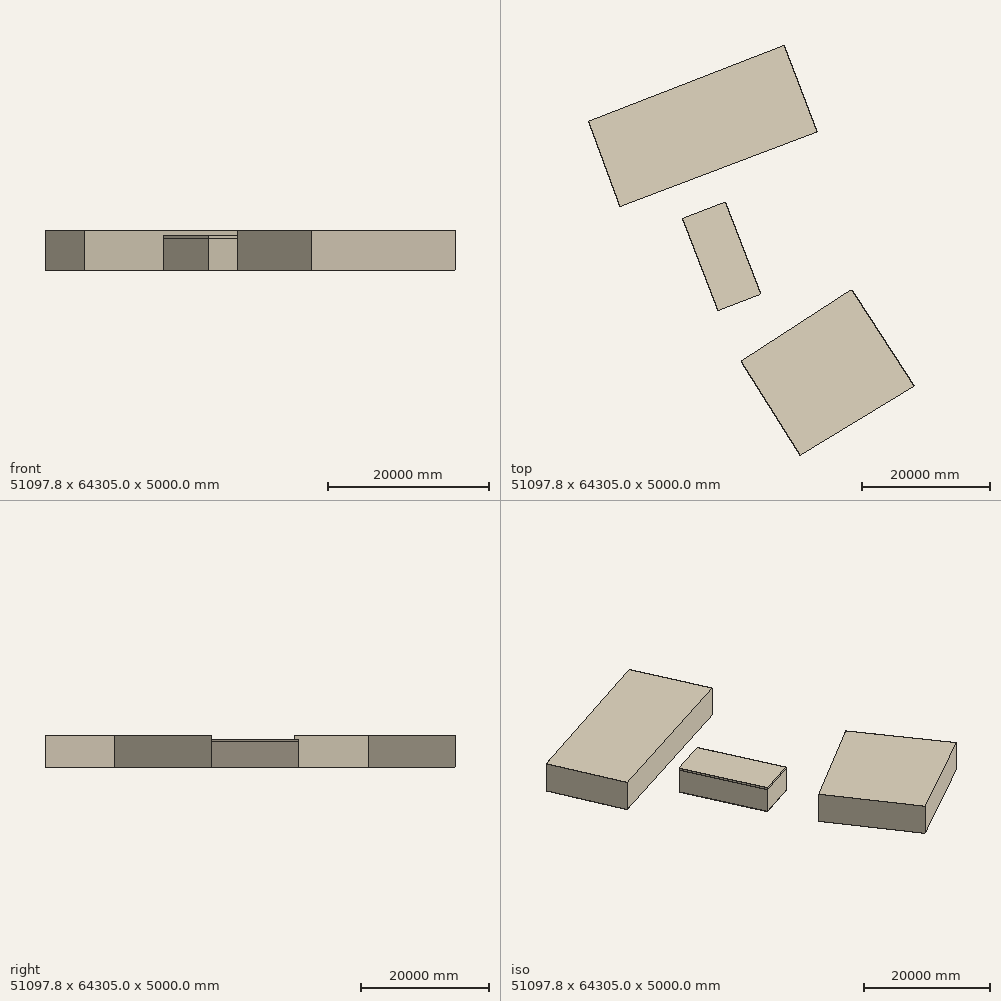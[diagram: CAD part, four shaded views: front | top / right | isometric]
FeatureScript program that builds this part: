
annotation { "Feature Type Name" : "Feature", "Feature Type Description" : "" }
export const myFeature = defineFeature(function(context is Context, id is Id, definition is map)
    precondition{}
    {
        {
            var Q0;
            Q0=qCreatedBy(makeId("Top.planeOp"),FACE);
            var sketch = newSketch(context, id + "F0", { "sketchPlane" : qUnion([Q0])});
            skLineSegment(sketch, "E0", {"start": v(-10158.18, -131.88) * mm, "end": v(9841.82, -131.88) * mm});
            skLineSegment(sketch, "E1", {"start": v(187539.75, 81737.34) * mm, "end": v(193121.23, 67288.97) * mm});
            skLineSegment(sketch, "E2", {"start": v(193121.23, 67288.97) * mm, "end": v(199849.27, 69888.05) * mm});
            skLineSegment(sketch, "E3", {"start": v(199849.27, 69888.05) * mm, "end": v(194267.79, 84336.42) * mm});
            skLineSegment(sketch, "E4", {"start": v(194267.79, 84336.42) * mm, "end": v(187539.75, 81737.34) * mm});
            skLineSegment(sketch, "E5", {"start": v(208669.68, 95326.9) * mm, "end": v(177736.31, 83607) * mm});
            skLineSegment(sketch, "E6", {"start": v(177736.31, 83607) * mm, "end": v(172814.6, 96986.59) * mm});
            skLineSegment(sketch, "E7", {"start": v(172814.6, 96986.59) * mm, "end": v(203493.68, 108899.4) * mm});
            skLineSegment(sketch, "E8", {"start": v(203493.68, 108899.4) * mm, "end": v(208669.68, 95326.9) * mm});
            skLineSegment(sketch, "E9", {"start": v(175795.11, 83973.93) * mm, "end": v(183542.53, 63918.76) * mm, "construction": true});
            skLineSegment(sketch, "E10", {"start": v(180970.64, 84832.4) * mm, "end": v(187893.07, 65474.8) * mm, "construction": true});
            skLineSegment(sketch, "E11", {"start": v(170830.15, 81002.61) * mm, "end": v(178579.4, 61691.7) * mm, "construction": true});
            skLineSegment(sketch, "E12", {"start": v(193121.23, 67288.97) * mm, "end": v(194231.34, 63706.36) * mm, "construction": true});
            skLineSegment(sketch, "E13", {"start": v(194231.34, 63706.36) * mm, "end": v(179655.72, 58700.32) * mm, "construction": true});
            skLineSegment(sketch, "E14", {"start": v(179655.72, 58700.32) * mm, "end": v(178466.66, 61613.23) * mm, "construction": true});
            skLineSegment(sketch, "E15", {"start": v(178466.66, 61613.23) * mm, "end": v(178579.4, 61691.7) * mm, "construction": true});
            skLineSegment(sketch, "E16", {"start": v(196729.08, 59349.96) * mm, "end": v(214079.01, 70606.48) * mm});
            skLineSegment(sketch, "E17", {"start": v(214079.01, 70606.48) * mm, "end": v(223912.44, 55450) * mm});
            skLineSegment(sketch, "E18", {"start": v(223912.44, 55450) * mm, "end": v(206013.89, 44594.36) * mm});
            skLineSegment(sketch, "E19", {"start": v(206013.89, 44594.36) * mm, "end": v(196729.08, 59349.96) * mm});
            skLineSegment(sketch, "E20", {"start": v(208670.5, 45709.94) * mm, "end": v(190801.62, 34997.4) * mm, "construction": true});
            skLineSegment(sketch, "E21", {"start": v(190801.62, 34997.4) * mm, "end": v(178771.96, 39826.82) * mm, "construction": true});
            skLineSegment(sketch, "E22", {"start": v(178771.96, 39826.82) * mm, "end": v(151260.15, 102166) * mm, "construction": true});
            skLineSegment(sketch, "E23", {"start": v(151260.15, 102166) * mm, "end": v(156670.24, 107744.42) * mm, "construction": true});
            skLineSegment(sketch, "E24", {"start": v(156670.24, 107744.42) * mm, "end": v(159799.36, 111734.04) * mm, "construction": true});
            skLineSegment(sketch, "E25", {"start": v(159799.36, 111734.04) * mm, "end": v(161481.26, 114667.59) * mm, "construction": true});
            skLineSegment(sketch, "E26", {"start": v(161481.26, 114667.59) * mm, "end": v(163124.04, 117483.79) * mm, "construction": true});
            skLineSegment(sketch, "E27", {"start": v(163124.04, 117483.79) * mm, "end": v(164917, 120674.92) * mm, "construction": true});
            skLineSegment(sketch, "E28", {"start": v(164917, 120674.92) * mm, "end": v(164917, 123686.68) * mm, "construction": true});
            skLineSegment(sketch, "E29", {"start": v(164917, 123686.68) * mm, "end": v(164643.2, 124762.32) * mm, "construction": true});
            skLineSegment(sketch, "E30", {"start": v(164643.2, 124762.32) * mm, "end": v(164643.2, 127206.94) * mm, "construction": true});
            skLineSegment(sketch, "E31", {"start": v(164643.2, 127206.94) * mm, "end": v(167061.37, 131699.1) * mm, "construction": true});
            skLineSegment(sketch, "E32", {"start": v(167061.37, 131699.1) * mm, "end": v(174739.8, 134962.66) * mm, "construction": true});
            skLineSegment(sketch, "E33", {"start": v(174739.8, 134962.66) * mm, "end": v(189157.47, 141112.01) * mm, "construction": true});
            skLineSegment(sketch, "E34", {"start": v(189157.47, 141112.01) * mm, "end": v(191512.92, 135589.46) * mm, "construction": true});
            skLineSegment(sketch, "E35", {"start": v(191512.92, 135589.46) * mm, "end": v(190598.55, 135199.47) * mm, "construction": true});
            skLineSegment(sketch, "E36", {"start": v(190598.55, 135199.47) * mm, "end": v(201688.16, 110933.7) * mm, "construction": true});
            skLineSegment(sketch, "E37", {"start": v(201688.16, 110933.7) * mm, "end": v(202729.39, 108955.99) * mm, "construction": true});
            skLineSegment(sketch, "E38", {"start": v(202729.39, 108955.99) * mm, "end": v(203642.8, 109310.67) * mm, "construction": true});
            skLineSegment(sketch, "E39", {"start": v(203642.8, 109310.67) * mm, "end": v(209361.07, 95181.4) * mm, "construction": true});
            skLineSegment(sketch, "E40", {"start": v(209361.07, 95181.4) * mm, "end": v(209730.67, 93234.83) * mm, "construction": true});
            skLineSegment(sketch, "E41", {"start": v(209730.67, 93234.83) * mm, "end": v(208728.07, 92845.51) * mm, "construction": true});
            skLineSegment(sketch, "E42", {"start": v(208728.07, 92845.51) * mm, "end": v(217027.5, 72191.76) * mm, "construction": true});
            skLineSegment(sketch, "E43", {"start": v(217027.5, 72191.76) * mm, "end": v(214271.76, 70679.21) * mm, "construction": true});
            skLineSegment(sketch, "E44", {"start": v(214271.76, 70679.21) * mm, "end": v(224345.41, 55221.25) * mm, "construction": true});
            skLineSegment(sketch, "E45", {"start": v(224345.41, 55221.25) * mm, "end": v(208670.5, 45709.94) * mm, "construction": true});
            skLineSegment(sketch, "E46", {"start": v(187539.75, 81737.34) * mm, "end": v(185689.7, 86620.34) * mm});
            skLineSegment(sketch, "E47", {"start": v(194267.79, 84336.42) * mm, "end": v(192434.3, 89175.7) * mm});
            skSolve(sketch);
        }
        {
            var Q0;
            Q0=makeQuery(id+"F0.imprint","IMPRINT",FACE,{"disambiguationData":[TD([[makeQuery(id+"F0.imprint","IMPRINT",EDGE,{"derivedFrom":sQuery(id+"F0.wireOp",EDGE,"E1")}),1.0]])]});
            extrude(context, id + "F1", {"entities" : qUnion([Q0]), "depth" : 50 * mm, "offsetDistance" : 25 * mm});
        }
        {
            var Q0;
            Q0=makeQuery(id+"F1.opExtrude","CAP_FACE",FACE,{"disambiguationData":[OSD([sQuery(id+"F0.wireOp",EDGE,"E1"),sQuery(id+"F0.wireOp",EDGE,"E2"),sQuery(id+"F0.wireOp",EDGE,"E3"),sQuery(id+"F0.wireOp",EDGE,"E4")])],"isStart":false});
            var sketch = newSketch(context, id + "F2", { "sketchPlane" : qUnion([Q0])});
            skLineSegment(sketch, "E48", {"start": v(194267.79, 84336.42) * mm, "end": v(199849.27, 69888.05) * mm});
            skLineSegment(sketch, "E49", {"start": v(199849.27, 69888.05) * mm, "end": v(193121.23, 67288.97) * mm});
            skLineSegment(sketch, "E50", {"start": v(193121.23, 67288.97) * mm, "end": v(187539.75, 81737.34) * mm});
            skLineSegment(sketch, "E51", {"start": v(187539.75, 81737.34) * mm, "end": v(194267.79, 84336.42) * mm});
            skLineSegment(sketch, "E52.0", {"start": v(193327.32, 67754.52) * mm, "end": v(188005.29, 81531.26) * mm});
            skLineSegment(sketch, "E52.1", {"start": v(199383.73, 70094.14) * mm, "end": v(193327.32, 67754.52) * mm});
            skLineSegment(sketch, "E52.2", {"start": v(194061.7, 83870.88) * mm, "end": v(199383.73, 70094.14) * mm});
            skLineSegment(sketch, "E52.3", {"start": v(188005.29, 81531.26) * mm, "end": v(194061.7, 83870.88) * mm});
            skLineSegment(sketch, "E53", {"start": v(195186, 80960.5) * mm, "end": v(189129.59, 78620.87) * mm});
            skLineSegment(sketch, "E54.0", {"start": v(195142.76, 81072.43) * mm, "end": v(189086.35, 78732.8) * mm});
            skLineSegment(sketch, "E55", {"start": v(192251.03, 79955.34) * mm, "end": v(191169.97, 82753.79) * mm});
            skLineSegment(sketch, "E56.0", {"start": v(192139.09, 79912.1) * mm, "end": v(191058.03, 82710.55) * mm});
            skSolve(sketch);
        }
        {
            var Q0;
            Q0=makeQuery(id+"F2.imprint","IMPRINT",FACE,{"disambiguationData":[TD([[makeQuery(id+"F2.imprint","IMPRINT",EDGE,{"derivedFrom":sQuery(id+"F2.wireOp",EDGE,"E48")}),1.0]])]});
            extrude(context, id + "F3", {"entities" : qUnion([Q0]), "depth" : 4000 * mm, "offsetDistance" : 25 * mm});
        }
        {
            var Q0;
            Q0=makeQuery(id+"F3.opExtrude","CAP_FACE",FACE,{"disambiguationData":[OSD([sQuery(id+"F2.wireOp",EDGE,"E48"),sQuery(id+"F2.wireOp",EDGE,"E49"),sQuery(id+"F2.wireOp",EDGE,"E50"),sQuery(id+"F2.wireOp",EDGE,"E51"),sQuery(id+"F2.wireOp",EDGE,"E52.0"),sQuery(id+"F2.wireOp",EDGE,"E52.1"),sQuery(id+"F2.wireOp",EDGE,"E52.2"),sQuery(id+"F2.wireOp",EDGE,"E52.3")])],"isStart":false});
            var sketch = newSketch(context, id + "F4", { "sketchPlane" : qUnion([Q0])});
            skLineSegment(sketch, "E57", {"start": v(187539.75, 81737.34) * mm, "end": v(194267.79, 84336.42) * mm});
            skLineSegment(sketch, "E58", {"start": v(194267.79, 84336.42) * mm, "end": v(199849.27, 69888.05) * mm});
            skLineSegment(sketch, "E59", {"start": v(199849.27, 69888.05) * mm, "end": v(193121.23, 67288.97) * mm});
            skLineSegment(sketch, "E60", {"start": v(193121.23, 67288.97) * mm, "end": v(187539.75, 81737.34) * mm});
            skSolve(sketch);
        }
        {
            var Q0;
            Q0 = qSketchRegion(id + "F4", true);
            extrude(context, id + "F5", {"entities" : qUnion([Q0]), "depth" : 360 * mm, "offsetDistance" : 25 * mm});
        }
        {
            var Q0;
            Q0=makeQuery(id+"F3.opExtrude","SWEPT_FACE",FACE,{"disambiguationData":[OSD([sQuery(id+"F2.wireOp",EDGE,"E51")])]});
            var sketch = newSketch(context, id + "F6", { "sketchPlane" : qUnion([Q0])});
            skLineSegment(sketch, "E61.bottom", {"start": v(-205994.37, 2050) * mm, "end": v(-204994.37, 2050) * mm});
            skLineSegment(sketch, "E61.top", {"start": v(-205994.37, 50) * mm, "end": v(-204994.37, 50) * mm});
            skLineSegment(sketch, "E61.left", {"start": v(-205994.37, 2050) * mm, "end": v(-205994.37, 50) * mm});
            skLineSegment(sketch, "E61.right", {"start": v(-204994.37, 2050) * mm, "end": v(-204994.37, 50) * mm});
            skSolve(sketch);
        }
        {
            var Q0;
            Q0 = qSketchRegion(id + "F6", true);
            extrude(context, id + "F7", {"entities" : qUnion([Q0]), "operationType" : NewBodyOperationType.REMOVE, "oppositeDirection" : true, "depth" : 360 * mm, "offsetDistance" : 25 * mm});
        }
        {
            var Q0;
            {var subQ0=sQuery(id+"F2.wireOp",EDGE,"E53");Q0=makeQuery(id+"F2.imprint","IMPRINT",FACE,{"disambiguationData":[TD([[makeQuery(id+"F2.imprint","IMPRINT",EDGE,{"derivedFrom":subQ0}),-1.0]])]});}
            var Q1;
            {var subQ0=sQuery(id+"F2.wireOp",EDGE,"E55");Q1=makeQuery(id+"F2.imprint","IMPRINT",FACE,{"disambiguationData":[TD([[makeQuery(id+"F2.imprint","IMPRINT",EDGE,{"derivedFrom":subQ0}),1.0]])]});}
            extrude(context, id + "F8", {"entities" : qUnion([Q0, Q1]), "depth" : 2400 * mm, "offsetDistance" : 25 * mm});
        }
        {
            var Q0;
            Q0=makeQuery(id+"F8.opExtrude","CAP_FACE",FACE,{"disambiguationData":[OSD([sQuery(id+"F2.wireOp",EDGE,"E52.0"),sQuery(id+"F2.wireOp",EDGE,"E52.2"),sQuery(id+"F2.wireOp",EDGE,"E53"),sQuery(id+"F2.wireOp",EDGE,"E54.0")])],"isStart":false});
            var sketch = newSketch(context, id + "F9", { "sketchPlane" : qUnion([Q0])});
            skLineSegment(sketch, "E62", {"start": v(195186, 80960.5) * mm, "end": v(189129.59, 78620.87) * mm});
            skLineSegment(sketch, "E63", {"start": v(195186, 80960.5) * mm, "end": v(194061.7, 83870.88) * mm});
            skLineSegment(sketch, "E64", {"start": v(194061.7, 83870.88) * mm, "end": v(188005.29, 81531.26) * mm});
            skLineSegment(sketch, "E65", {"start": v(188005.29, 81531.26) * mm, "end": v(189129.59, 78620.87) * mm});
            skSolve(sketch);
        }
        {
            var Q0;
            Q0 = qSketchRegion(id + "F9", true);
            extrude(context, id + "F10", {"entities" : qUnion([Q0]), "depth" : 200 * mm, "offsetDistance" : 25 * mm});
        }
        {
            var Q0;
            Q0=makeQuery(id+"F8.opExtrude","SWEPT_FACE",FACE,{"disambiguationData":[OSD([sQuery(id+"F2.wireOp",EDGE,"E53")])]});
            var sketch = newSketch(context, id + "F11", { "sketchPlane" : qUnion([Q0])});
            skLineSegment(sketch, "E66.bottom", {"start": v(205054.37, 50) * mm, "end": v(206054.37, 50) * mm});
            skLineSegment(sketch, "E66.top", {"start": v(205054.37, 2050) * mm, "end": v(206054.37, 2050) * mm});
            skLineSegment(sketch, "E66.left", {"start": v(205054.37, 50) * mm, "end": v(205054.37, 2050) * mm});
            skLineSegment(sketch, "E66.right", {"start": v(206054.37, 50) * mm, "end": v(206054.37, 2050) * mm});
            skLineSegment(sketch, "E67.bottom", {"start": v(209446.98, 50) * mm, "end": v(208446.98, 50) * mm});
            skLineSegment(sketch, "E67.top", {"start": v(209446.98, 2050) * mm, "end": v(208446.98, 2050) * mm});
            skLineSegment(sketch, "E67.left", {"start": v(209446.98, 50) * mm, "end": v(209446.98, 2050) * mm});
            skLineSegment(sketch, "E67.right", {"start": v(208446.98, 50) * mm, "end": v(208446.98, 2050) * mm});
            skSolve(sketch);
        }
        {
            var Q0;
            Q0 = qSketchRegion(id + "F11", true);
            extrude(context, id + "F12", {"entities" : qUnion([Q0]), "operationType" : NewBodyOperationType.REMOVE, "oppositeDirection" : true, "depth" : 120 * mm, "offsetDistance" : 25 * mm});
        }
        {
            var Q0;
            Q0=makeQuery(id+"F0.imprint","IMPRINT",FACE,{"disambiguationData":[TD([[makeQuery(id+"F0.imprint","IMPRINT",EDGE,{"derivedFrom":sQuery(id+"F0.wireOp",EDGE,"E16")}),-1.0]])]});
            extrude(context, id + "F13", {"entities" : qUnion([Q0]), "depth" : 5000 * mm, "offsetDistance" : 25 * mm});
        }
        {
            var Q0;
            {var subQ0=sQuery(id+"F0.wireOp",EDGE,"E6");Q0=makeQuery(id+"F0.imprint","IMPRINT",FACE,{"disambiguationData":[TD([[makeQuery(id+"F0.imprint","IMPRINT",EDGE,{"derivedFrom":subQ0}),-1.0]])]});}
            extrude(context, id + "F14", {"entities" : qUnion([Q0]), "depth" : 5000 * mm, "offsetDistance" : 25 * mm});
        }
    });
